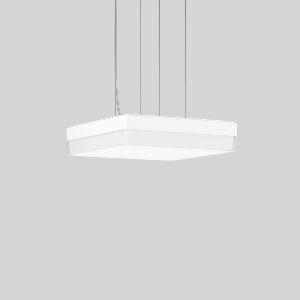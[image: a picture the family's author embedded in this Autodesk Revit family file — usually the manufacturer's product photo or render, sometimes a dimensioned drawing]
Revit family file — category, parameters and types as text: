
# Revit family: flat_slim_square_312542_002_730_6682
name_source: partatom
category: Lighting Fixtures
units: mm (PartAtom-declared; Revit-internal decimal feet)

## family parameters
Cut with Voids When Loaded = No
Host = Face
Light Source = No
Part Type = Normal
Room Calculation Point = No
Round Connector Dimension = Use Diameter
Shared = No

## types (1)
- MultiLumen 2 840 (1 x LED Modul 840, 2300 lm, 4000)
    Apparent Load = 21 VA
    CIE Flux Codes = 43 75 93 91 100
    Color Rendering = 80
    Color Temperature = 4000
    Default Elevation = 1800 mm
    Height = 70 mm
    Lamp = 1 x LED Modul 840
    Lamp Light Flux = 2300 lm
    Lamp count = 1
    Length = 300 mm
    Lifetime = 50000 h
    Luminous efficacy = 110 lm/W
    Manufacturer = RZB
    ModVariant = No
    Model = 312542.002.730
    Mounting Place = Ceiling
    Mounting Type = Pendant
    Number of Poles = 1
    OnlyDefault = Yes
    Power Factor = 1
    Product Name = FLAT SLIM square
    Product group = Pendant luminaires
    ProductGroupID = 902
    Protection Class = Protection class I
    Protection Degree = IP 40
    RLX_Detail_Level = 1
    RLX_Emergency_Light_Flux = 0 lm
    RLX_Emergency_Type = 0
    RLX_Emergency_Type_DB = No
    RlxData = <blob elided: 13861 chars, md5=1f0c635e>
    Socket = socket
    Standby Power = 0 W
    System Light Flux = 2300 lm
    System Power = 21 W
    Type Comments = MultiLumen 2 840
    Type Image = 312542.002.jpg
    URL = http://relux.com
    VarID = multilumen_2_840
    Voltage = 230 V
    Voltage Range = 220-240 V
    Weight = 0.00 kg
    Width = 300 mm

## geometry (parser evidence)
native form markers: Sweep x13
no freeform markers — native parametric forms only
